# Revit family: AKR245S
name_source: partatom
category: Structural Connections
revit_build: Autodesk Revit 2015 (Build: 20140606_1530(x64)
units: mm (PartAtom-declared; Revit-internal decimal feet)

## types (1)
- AKR245S
    Default Elevation = 0 mm  [stored 0 ft]
    Density = 0.49 kg
    Description = Holdowns
    EPD = https://www.strongtie.eu
    ETA / DoP = https://www.strongtie.eu
    Manufacturer = Simpson Strong-Tie
    Model = AKR245S
    Model Disclaimer = Contact Simpson Strong-Tie Company  for more information
    Model ID = 0240410424553273588985171392764023954810
    Name = AKR245S
    ObjectType = AKR245S
    Product Material = Stainless steel A4
    Product Type = Holdowns
    Reference = AKR245S
    Technical datasheet = https://www.strongtie.eu
    URL = www.strongtie.eu
    UniClass Number = Pr_20_29_31_13
    UniClass Title = Carbon steel punched metal plate fasteners

note: [stored X ft] marks values corroborated as IEEE doubles in the binary element streams (Revit-internal decimal feet)

## geometry (parser evidence)
native form markers: Blend x25, Sweep x3
no freeform markers — native parametric forms only
